# Revit family: 3001766 Sylvania Lighting Fixture INSTR SW IP44 REFLED BA WW DIM
name_source: partatom
category: Lighting Fixtures
revit_build: Autodesk Revit 2016 (Build: 20150220_1215(x64)
units: mm (PartAtom-declared; Revit-internal decimal feet)

## family parameters
Cut with Voids When Loaded = No
Host = Face
Light Source = No
OmniClass Number = 23.80.70.00
OmniClass Title = Lighting
Part Type = Normal
Room Calculation Point = No
Round Connector Dimension = Use Diameter
Shared = No

## types (1)
- 3001766 INSTR SW IP44 REFLED BA WW DIM
    Apparent Load = 6 VA
    Assembly Code = D5020200
    AssetType = Fixed
    ClassificationName = Uniclass2015
    ClassificationValue = EF_70_80
    Cost = 0 $
    Default Elevation = 1219 mm
    DimmingControlOptions = Dimmable
    DocumentationLiterature = http://www.sylvania-lighting.com
    DurationUnit = hours
    ExpectedLife = 50000
    HeightTrim_SYL = 4 mm  [stored 0.0131234 ft]
    IP44Version_SYL = Yes
    IfcExportAs = IfcLightFixtureType
    IfcExportType = IfcLightFixtureType
    ImpactProtectionIndex = IK02
    IngressProtection = IP20/44
    InputVoltage = 220-240V~
    Keynote = 16500
    Lamp = LED
    LampColourRenderingIndex = 80
    LampColourTemperature = 3000 K
    LampNominalLuminous = 345 lm
    LampsType = LED
    LightOutputRatio = 100
    LuminousEfficacy = 57.5 lm/W
    Manufacturer = Feilo Sylvania
    ManufacturerName = Feilo Sylvania
    Material = aluminium housing, plastic diffuser
    Material_1_FEILO = Body-Sylvania-Inset-BA
    Material_2_FEILO = <By Category>
    Material_3_FEILO = <By Category>
    Material_4_FEILO = <By Category>
    Model = INSTR SW IP44 REFLED BA WW DIM
    ModelNumber = 3001766
    ModelReference = INSTR SW IP44 REFLED BA WW DIM
    Name = INSTR SW IP44 REFLED BA WW DIM
    NominalDepth = 95 mm
    NominalHeight = 100 mm  [stored 0.328084 ft]
    NominalLength = 95 mm
    PowerConsumption = 6 W
    PowerFactor = 0
    RadiusTrimIn_SYL = 31 mm  [stored 0.101706 ft]
    RadiusTrim_SYL = 48 mm
    Type Image = <None>
    TypeHead_SYL = Inset Adjustable Head : 3001766 INSTR SW IP44 REFLED BA WW DIM
    TypeName = INSTR SW IP44 REFLED BA WW DIM
    URL = http://www.sylvania-lighting.com
    Voltage = 230 V
    Weight = 6.51 kg

note: [stored X ft] marks values corroborated as IEEE doubles in the binary element streams (Revit-internal decimal feet)

## geometry (parser evidence)
native form markers: Sweep x6
no freeform markers — native parametric forms only
